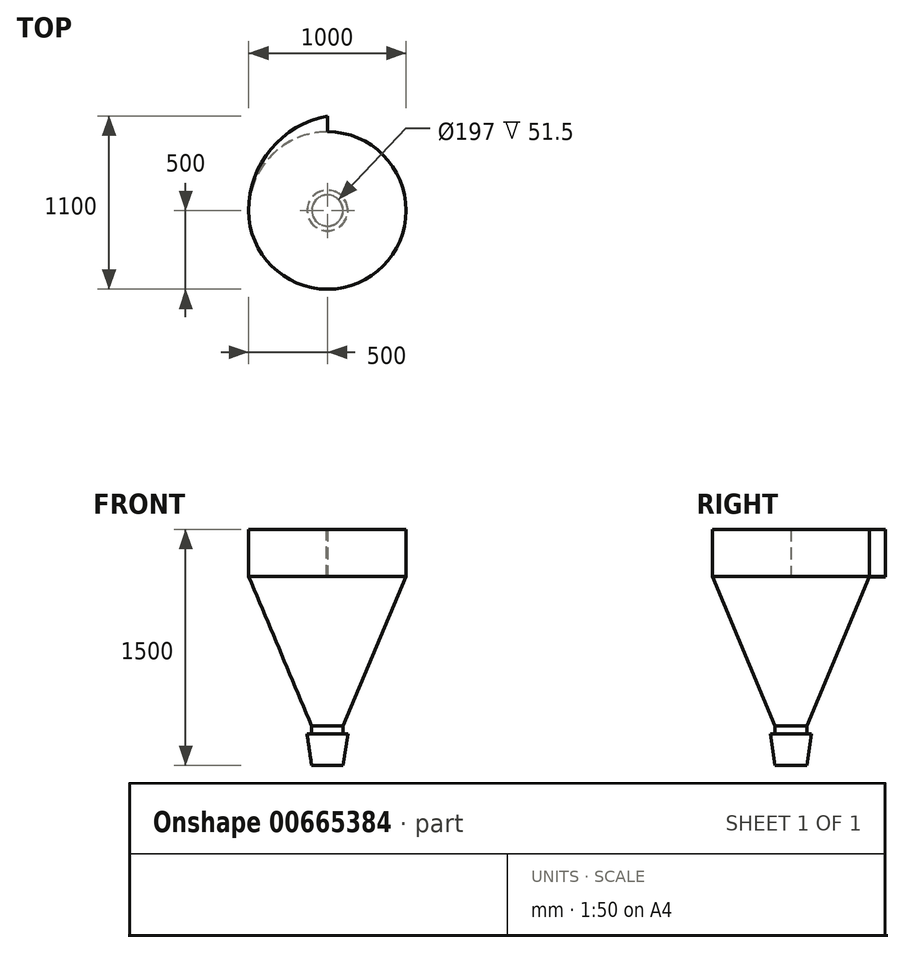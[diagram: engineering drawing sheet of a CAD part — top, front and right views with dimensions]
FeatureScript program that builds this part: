
annotation { "Feature Type Name" : "Feature", "Feature Type Description" : "" }
export const myFeature = defineFeature(function(context is Context, id is Id, definition is map)
    precondition{}
    {
        {
            var Q0;
            Q0=qCreatedBy(makeId("Front.planeOp"),FACE);
            var sketch = newSketch(context, id + "F0", { "sketchPlane" : qUnion([Q0])});
            skLineSegment(sketch, "E0", {"start": v(0, 1500) * mm, "end": v(500, 1500) * mm});
            skLineSegment(sketch, "E1", {"start": v(500, 1200) * mm, "end": v(500, 1500) * mm});
            skLineSegment(sketch, "E2", {"start": v(500, 1200) * mm, "end": v(100, 250) * mm});
            skLineSegment(sketch, "E3", {"start": v(100, 250) * mm, "end": v(100, 200) * mm});
            skLineSegment(sketch, "E4", {"start": v(100, 200) * mm, "end": v(130, 200) * mm});
            skLineSegment(sketch, "E5", {"start": v(130, 200) * mm, "end": v(100, 0) * mm});
            skLineSegment(sketch, "E6", {"start": v(100, 0) * mm, "end": v(0, 0) * mm});
            skLineSegment(sketch, "E7", {"start": v(0, 0) * mm, "end": v(0, 1500) * mm, "construction": true});
            skLineSegment(sketch, "E8", {"start": v(0, 0) * mm, "end": v(0, 1.5) * mm});
            skLineSegment(sketch, "E9", {"start": v(0, 1.5) * mm, "end": v(98.7, 1.5) * mm});
            skLineSegment(sketch, "E10", {"start": v(98.7, 1.5) * mm, "end": v(128.26, 198.5) * mm});
            skLineSegment(sketch, "E11", {"start": v(128.26, 198.5) * mm, "end": v(98.5, 198.5) * mm});
            skLineSegment(sketch, "E12", {"start": v(98.5, 198.5) * mm, "end": v(98.5, 250) * mm});
            skLineSegment(sketch, "E13", {"start": v(98.5, 250) * mm, "end": v(498.5, 1200) * mm});
            skLineSegment(sketch, "E14", {"start": v(498.5, 1200) * mm, "end": v(498.5, 1498.5) * mm});
            skLineSegment(sketch, "E15", {"start": v(498.5, 1498.5) * mm, "end": v(0, 1498.5) * mm});
            skLineSegment(sketch, "E16", {"start": v(0, 1498.5) * mm, "end": v(0, 1500) * mm});
            skSolve(sketch);
        }
        {
            var Q0;
            Q0 = qSketchRegion(id + "F0", true);
            var Q1;
            Q1=sQuery(id+"F0.wireOp",EDGE,"E7");
            revolve(context, id + "F1", {"entities" : qUnion([Q0]), "axis" : qUnion([Q1]), "revolveType" : RevolveType.FULL});
        }
        {
            var Q0;
            Q0=makeQuery(id+"F1.opRevolve","SWEPT_FACE",FACE,{"disambiguationData":[OSD([sQuery(id+"F0.wireOp",EDGE,"E0")])]});
            var sketch = newSketch(context, id + "F2", { "sketchPlane" : qUnion([Q0])});
            skCircle(sketch, "E17.0", {"center": v(0, 0) * mm, "radius": 500 * mm, "construction": true});
            skLineSegment(sketch, "E18", {"start": v(0, 0) * mm, "end": v(0, -500) * mm, "construction": true});
            skLineSegment(sketch, "E19", {"start": v(0, 0) * mm, "end": v(0, 500) * mm, "construction": true});
            skLineSegment(sketch, "E20", {"start": v(0, 0) * mm, "end": v(-500, 0) * mm, "construction": true});
            skLineSegment(sketch, "E21", {"start": v(0, 0) * mm, "end": v(500, 0) * mm, "construction": true});
            skSolve(sketch);
        }
        {
            var Q0;
            Q0=makeQuery(id+"F2.imprint","IMPRINT",FACE,{"disambiguationData":[TD([[makeQuery(id+"F2.imprint","IMPRINT",EDGE,{"derivedFrom":makeQuery(id+"F1.opRevolve","SWEPT_EDGE",EDGE,{"disambiguationData":[OSD([sQuery(id+"F0.wireOp",EDGE,"E0"),sQuery(id+"F0.wireOp",EDGE,"E1")])]})}),-1.0]])]});
            var sketch = newSketch(context, id + "F3", { "sketchPlane" : qUnion([Q0])});
            skArc(sketch, "E22", {"start": v(0, 600) * mm, "mid": v(-358.61, 390.51) * mm, "end": v(-500, 0) * mm});
            skSolve(sketch);
        }
        {
            var Q0;
            Q0=sQuery(id+"F2.wireOp",VERTEX,"E19.end");
            var Q1;
            Q1=qCreatedBy(makeId("Right.planeOp"),FACE);
            cPlane(context, id + "F4", {"entities" : qUnion([Q0, Q1]), "cplaneType" : CPlaneType.PLANE_POINT, "offset" : 25 * mm, "width" : 150 * mm, "height" : 150 * mm});
        }
        {
            var Q0;
            Q0=qCreatedBy(id+"F4.planeOp",FACE);
            var sketch = newSketch(context, id + "F5", { "sketchPlane" : qUnion([Q0])});
            skPoint(sketch, "E23.0", {"position": v(500, 1500) * mm});
            skLineSegment(sketch, "E24.bottom", {"start": v(500, 1500) * mm, "end": v(600, 1500) * mm});
            skLineSegment(sketch, "E24.top", {"start": v(500, 1200) * mm, "end": v(600, 1200) * mm});
            skLineSegment(sketch, "E24.left", {"start": v(500, 1500) * mm, "end": v(500, 1200) * mm});
            skLineSegment(sketch, "E24.right", {"start": v(600, 1500) * mm, "end": v(600, 1200) * mm});
            skSolve(sketch);
        }
        {
            var Q0;
            Q0=makeQuery(id+"F5.imprint","IMPRINT",FACE,{"disambiguationData":[TD([[makeQuery(id+"F5.imprint","IMPRINT",EDGE,{"derivedFrom":sQuery(id+"F5.wireOp",EDGE,"E24.bottom")}),-1.0]])]});
            var Q1;
            Q1 = qConstructionFilter(qBodyType(qCreatedBy(id + "F3" ,EDGE), BodyType.WIRE), ConstructionObject.NO);
            sweep(context, id + "F6", {"operationType" : NewBodyOperationType.REMOVE, "profiles" : qUnion([Q0]), "path" : qUnion([Q1])});
        }
        {
            var Q0;
            Q0=qCreatedBy(id+"F4.planeOp",FACE);
            var sketch = newSketch(context, id + "F7", { "sketchPlane" : qUnion([Q0])});
            skPoint(sketch, "E25.0", {"position": v(500, 1500) * mm});
            skLineSegment(sketch, "E26.0", {"start": v(500, 1500) * mm, "end": v(600, 1500) * mm});
            skLineSegment(sketch, "E26.1", {"start": v(600, 1500) * mm, "end": v(600, 1200) * mm});
            skLineSegment(sketch, "E27", {"start": v(500, 1500) * mm, "end": v(500, 1498.5) * mm});
            skLineSegment(sketch, "E28", {"start": v(500, 1498.5) * mm, "end": v(598.5, 1498.5) * mm});
            skLineSegment(sketch, "E29", {"start": v(598.5, 1498.5) * mm, "end": v(598.5, 1200) * mm});
            skLineSegment(sketch, "E30", {"start": v(598.5, 1200) * mm, "end": v(600, 1200) * mm});
            skSolve(sketch);
        }
        {
            var Q0;
            Q0 = qSketchRegion(id + "F7", true);
            var Q1;
            Q1=sQuery(id+"F3.wireOp",EDGE,"E22");
            sweep(context, id + "F8", {"operationType" : NewBodyOperationType.ADD, "profiles" : qUnion([Q0]), "path" : qUnion([Q1])});
        }
        {
            var Q0;
            Q0=sQuery(id+"F5.wireOp",VERTEX,"E24.right.end");
            var Q1;
            Q1=qCreatedBy(makeId("Top.planeOp"),FACE);
            cPlane(context, id + "F9", {"entities" : qUnion([Q0, Q1]), "cplaneType" : CPlaneType.PLANE_POINT, "offset" : 25 * mm, "width" : 150 * mm, "height" : 150 * mm});
        }
        {
            var Q0;
            Q0=qCreatedBy(id+"F9.planeOp",FACE);
            var sketch = newSketch(context, id + "F10", { "sketchPlane" : qUnion([Q0])});
            skPoint(sketch, "E31.0", {"position": v(0, 500) * mm});
            skArc(sketch, "E32.0", {"start": v(0, 600) * mm, "mid": v(-358.61, 390.51) * mm, "end": v(-500, 0) * mm});
            skArc(sketch, "E33", {"start": v(0, 500) * mm, "mid": v(-353.55, 353.55) * mm, "end": v(-500, 0) * mm});
            skLineSegment(sketch, "E34", {"start": v(0, 500) * mm, "end": v(0, 600) * mm});
            skSolve(sketch);
        }
        {
            var Q0;
            Q0 = qSketchRegion(id + "F10", true);
            extrude(context, id + "F11", {"entities" : qUnion([Q0]), "oppositeDirection" : true, "depth" : 1.5 * mm, "offsetDistance" : 25 * mm});
        }
    });
